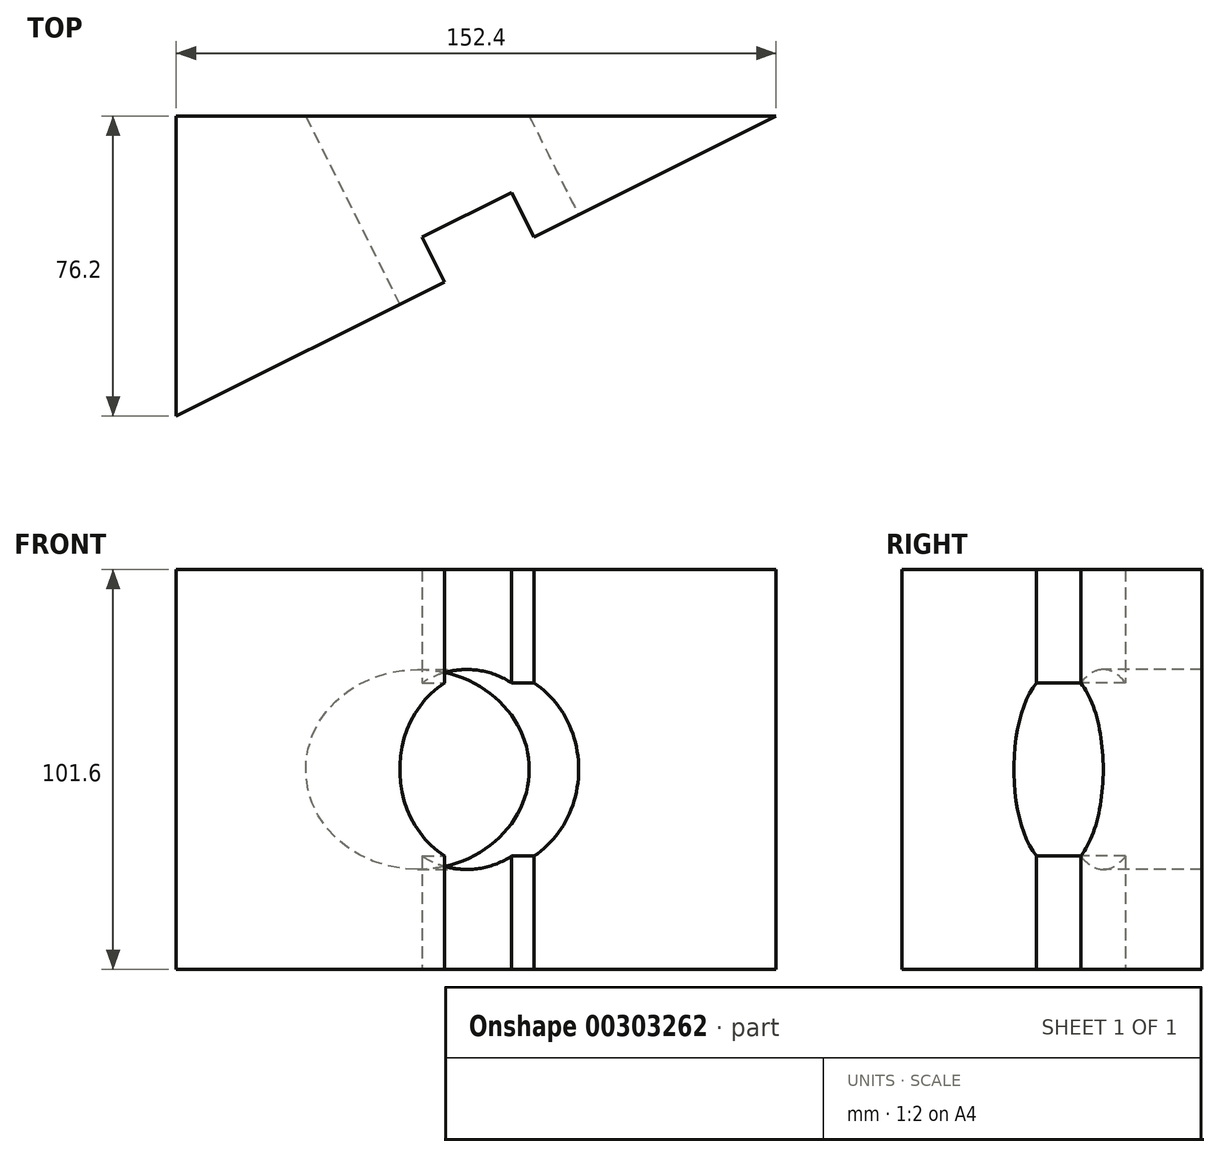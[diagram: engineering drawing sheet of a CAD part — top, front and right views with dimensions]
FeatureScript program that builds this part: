
annotation { "Feature Type Name" : "Feature", "Feature Type Description" : "" }
export const myFeature = defineFeature(function(context is Context, id is Id, definition is map)
    precondition{}
    {
        {
            var Q0;
            Q0=qCreatedBy(makeId("Top.planeOp"),FACE);
            var sketch = newSketch(context, id + "F0", { "sketchPlane" : qUnion([Q0])});
            skLineSegment(sketch, "E0.bottom", {"start": v(0, 0) * mm, "end": v(152.4, 0) * mm});
            skLineSegment(sketch, "E0.top", {"start": v(0, 76.2) * mm, "end": v(152.4, 76.2) * mm});
            skLineSegment(sketch, "E0.left", {"start": v(0, 0) * mm, "end": v(0, 76.2) * mm});
            skLineSegment(sketch, "E0.right", {"start": v(152.4, 0) * mm, "end": v(152.4, 76.2) * mm});
            skLineSegment(sketch, "E1", {"start": v(0, 0) * mm, "end": v(152.4, 76.2) * mm});
            skSolve(sketch);
        }
        {
            var Q0;
            Q0=makeQuery(id+"F0.imprint","IMPRINT",FACE,{"disambiguationData":[TD([[makeQuery(id+"F0.imprint","IMPRINT",EDGE,{"derivedFrom":sQuery(id+"F0.wireOp",EDGE,"E0.top")}),-1.0]])]});
            extrude(context, id + "F1", {"entities" : qUnion([Q0]), "depth" : 101.6 * mm});
        }
        {
            var Q0;
            Q0=makeQuery(id+"F1.opExtrude","SWEPT_FACE",FACE,{"disambiguationData":[OSD([sQuery(id+"F0.wireOp",EDGE,"E1")])]});
            var sketch = newSketch(context, id + "F2", { "sketchPlane" : qUnion([Q0])});
            skLineSegment(sketch, "E2.bottom", {"start": v(101.6, 101.6) * mm, "end": v(76.2, 101.6) * mm});
            skLineSegment(sketch, "E2.top", {"start": v(101.6, 0) * mm, "end": v(76.2, 0) * mm});
            skLineSegment(sketch, "E2.left", {"start": v(101.6, 101.6) * mm, "end": v(101.6, 0) * mm});
            skLineSegment(sketch, "E2.right", {"start": v(76.2, 101.6) * mm, "end": v(76.2, 0) * mm});
            skPoint(sketch, "E2.middle", {"position": v(88.9, 50.8) * mm});
            skSolve(sketch);
        }
        {
            var Q0;
            Q0=makeQuery(id+"F2.imprint","IMPRINT",FACE,{"disambiguationData":[TD([[makeQuery(id+"F2.imprint","IMPRINT",EDGE,{"derivedFrom":sQuery(id+"F2.wireOp",EDGE,"E2.bottom")}),-1.0]])]});
            extrude(context, id + "F3", {"entities" : qUnion([Q0]), "operationType" : NewBodyOperationType.REMOVE, "oppositeDirection" : true, "depth" : 12.7 * mm});
        }
        {
            var Q0;
            {var subQ0=sQuery(id+"F2.wireOp",EDGE,"E2.right");Q0=makeQuery(id+"F2.imprint","IMPRINT",FACE,{"disambiguationData":[TD([[makeQuery(id+"F2.imprint","IMPRINT",EDGE,{"derivedFrom":subQ0}),-1.0]])]});}
            var sketch = newSketch(context, id + "F4", { "sketchPlane" : qUnion([Q0])});
            skCircle(sketch, "E3", {"center": v(88.9, 50.8) * mm, "radius": 25.4 * mm});
            skSolve(sketch);
        }
        {
            var Q0;
            {var subQ0=sQuery(id+"F4.wireOp",EDGE,"E3");var subQ1=makeQuery(id+"F2.imprint","IMPRINT",EDGE,{"derivedFrom":sQuery(id+"F2.wireOp",EDGE,"E2.right")});var subQ2=makeQuery(id+"F4.imprint","INTERSECT",VERTEX,{"disambiguationData":[OD(0.0)],"derivedFrom":[subQ1,subQ0]});Q0=makeQuery(id+"F4.imprint","IMPRINT",FACE,{"disambiguationData":[TD([[makeQuery(id+"F4.imprint","IMPRINT",EDGE,{"disambiguationData":[TD([[subQ2,1.0]])],"derivedFrom":subQ0}),1.0]])]});}
            var Q1;
            {var subQ0=sQuery(id+"F4.wireOp",EDGE,"E3");var subQ1=makeQuery(id+"F2.imprint","IMPRINT",EDGE,{"derivedFrom":sQuery(id+"F2.wireOp",EDGE,"E2.right")});var subQ2=makeQuery(id+"F4.imprint","INTERSECT",VERTEX,{"disambiguationData":[OD(0.0)],"derivedFrom":[subQ1,subQ0]});Q1=makeQuery(id+"F4.imprint","IMPRINT",FACE,{"disambiguationData":[TD([[makeQuery(id+"F4.imprint","IMPRINT",EDGE,{"disambiguationData":[TD([[subQ2,-1.0]])],"derivedFrom":subQ0}),1.0]])]});}
            extrude(context, id + "F5", {"entities" : qUnion([Q0, Q1]), "operationType" : NewBodyOperationType.REMOVE, "endBound" : BoundingType.THROUGH_ALL, "oppositeDirection" : true, "depth" : 25.4 * mm});
        }
    });
